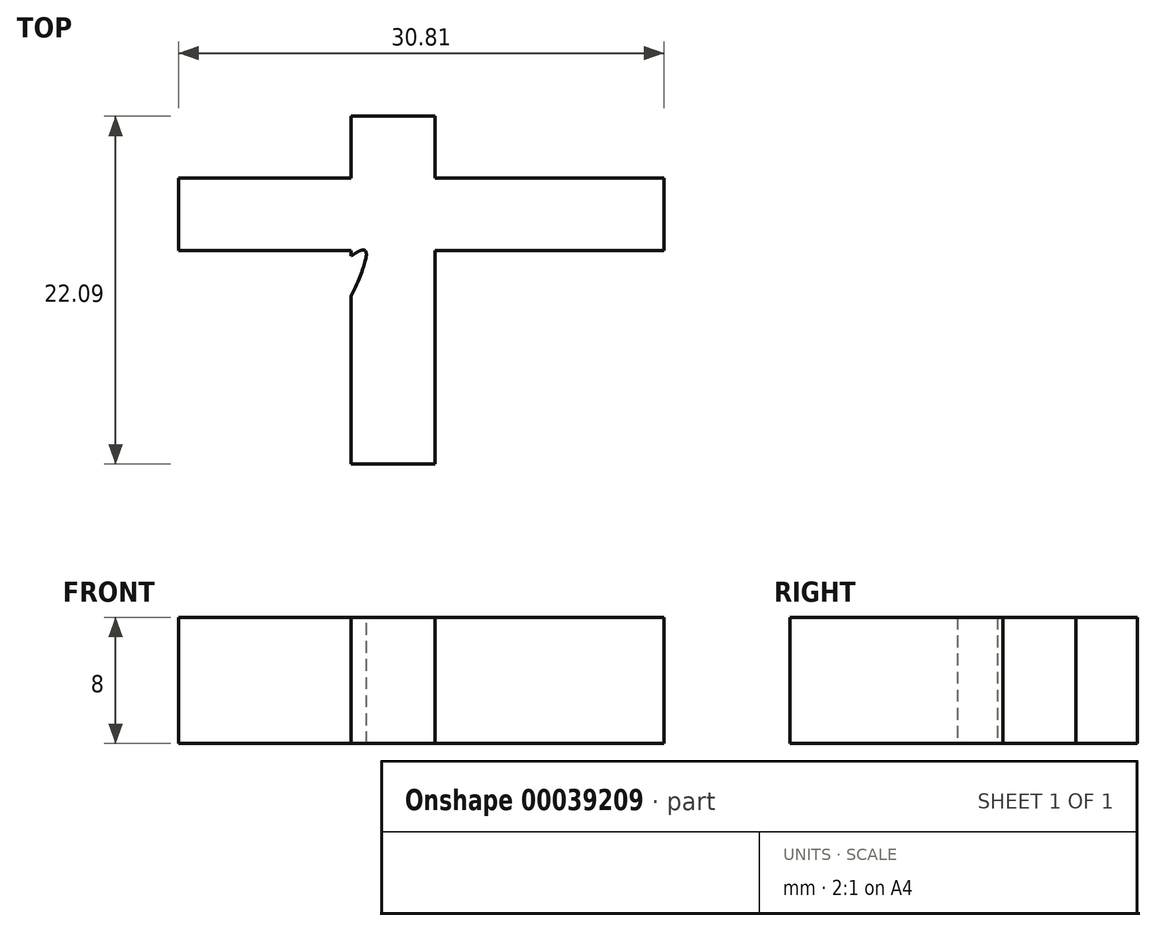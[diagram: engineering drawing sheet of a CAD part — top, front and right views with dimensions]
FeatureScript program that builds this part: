
annotation { "Feature Type Name" : "Feature", "Feature Type Description" : "" }
export const myFeature = defineFeature(function(context is Context, id is Id, definition is map)
    precondition{}
    {
        {
            var Q0;
            Q0=qCreatedBy(makeId("Top.planeOp"),FACE);
            var sketch = newSketch(context, id + "F0", { "sketchPlane" : qUnion([Q0])});
            skLineSegment(sketch, "E0.bottom", {"start": v(-13.7, 22.5) * mm, "end": v(17.11, 22.5) * mm});
            skLineSegment(sketch, "E0.top", {"start": v(-13.7, 17.89) * mm, "end": v(17.11, 17.89) * mm});
            skLineSegment(sketch, "E0.left", {"start": v(-13.7, 22.5) * mm, "end": v(-13.7, 17.89) * mm});
            skLineSegment(sketch, "E0.right", {"start": v(17.11, 22.5) * mm, "end": v(17.11, 17.89) * mm});
            skLineSegment(sketch, "E1.bottom", {"start": v(-2.74, 26.43) * mm, "end": v(2.59, 26.43) * mm});
            skLineSegment(sketch, "E1.top", {"start": v(-2.74, 4.34) * mm, "end": v(2.59, 4.34) * mm});
            skLineSegment(sketch, "E1.left", {"start": v(-2.74, 26.43) * mm, "end": v(-2.74, 4.34) * mm});
            skLineSegment(sketch, "E1.right", {"start": v(2.59, 26.43) * mm, "end": v(2.59, 4.34) * mm});
            skPoint(sketch, "E2.0.internal.snap0", {"position": v(-2.74, 15.39) * mm});
            skFitSpline(sketch, "E3.MirrorC", {"points": [v(1.84, 17.89) * mm, v(8.57, 12.75) * mm, v(13.7, 8.64) * mm, v(11.13, 5.56) * mm, v(6.51, 8.64) * mm, v(1.84, 17.89) * mm]});
            skPoint(sketch, "E4.MirrorP", {"position": v(2.74, 15.39) * mm});
            skFitSpline(sketch, "E5.MirrorC", {"points": [v(-1.84, 17.89) * mm, v(-8.57, 12.75) * mm, v(-13.7, 8.64) * mm, v(-11.13, 5.56) * mm, v(-6.51, 8.64) * mm, v(-1.84, 17.89) * mm]});
            skSolve(sketch);
        }
        {
            var Q0;
            {var subQ0=sQuery(id+"F0.wireOp",EDGE,"E1.left");var subQ3=sQuery(id+"F0.wireOp",EDGE,"E0.bottom");var subQ4=makeQuery(id+"F0.imprint","INTERSECT",VERTEX,{"derivedFrom":[subQ3,subQ0]});Q0=makeQuery(id+"F0.imprint","IMPRINT",FACE,{"disambiguationData":[TD([[makeQuery(id+"F0.imprint","IMPRINT",EDGE,{"disambiguationData":[TD([[subQ4,-1.0]])],"derivedFrom":subQ3}),-1.0]])]});}
            var Q1;
            {var subQ3=sQuery(id+"F0.wireOp",EDGE,"E1.bottom");Q1=makeQuery(id+"F0.imprint","IMPRINT",FACE,{"disambiguationData":[TD([[makeQuery(id+"F0.imprint","IMPRINT",EDGE,{"derivedFrom":subQ3}),-1.0]])]});}
            var Q2;
            {var subQ7=sQuery(id+"F0.wireOp",EDGE,"E0.left");Q2=makeQuery(id+"F0.imprint","IMPRINT",FACE,{"disambiguationData":[TD([[makeQuery(id+"F0.imprint","IMPRINT",EDGE,{"derivedFrom":subQ7}),1.0]])]});}
            var Q3;
            {var subQ1=sQuery(id+"F0.wireOp",EDGE,"E0.top");var subQ2=sQuery(id+"F0.wireOp",EDGE,"E2");var subQ5=makeQuery(id+"F0.imprint","INTERSECT",VERTEX,{"derivedFrom":[subQ1,subQ2]});Q3=makeQuery(id+"F0.imprint","IMPRINT",FACE,{"disambiguationData":[TD([[makeQuery(id+"F0.imprint","IMPRINT",EDGE,{"disambiguationData":[TD([[subQ5,-1.0]])],"derivedFrom":subQ2}),1.0]])]});}
            var Q4;
            {var subQ0=sQuery(id+"F0.wireOp",EDGE,"E3.MirrorC");var subQ1=sQuery(id+"F0.wireOp",EDGE,"E0.top");var subQ3=makeQuery(id+"F0.imprint","INTERSECT",VERTEX,{"disambiguationData":[OD(0.0)],"derivedFrom":[subQ1,subQ0]});Q4=makeQuery(id+"F0.imprint","IMPRINT",FACE,{"disambiguationData":[TD([[makeQuery(id+"F0.imprint","IMPRINT",EDGE,{"disambiguationData":[TD([[subQ3,-1.0]])],"derivedFrom":subQ1}),-1.0]])]});}
            var Q5;
            {var subQ8=sQuery(id+"F0.wireOp",EDGE,"E0.right");Q5=makeQuery(id+"F0.imprint","IMPRINT",FACE,{"disambiguationData":[TD([[makeQuery(id+"F0.imprint","IMPRINT",EDGE,{"derivedFrom":subQ8}),-1.0]])]});}
            var Q6;
            {var subQ0=sQuery(id+"F0.wireOp",EDGE,"E5.MirrorC");var subQ1=sQuery(id+"F0.wireOp",EDGE,"E1.left");var subQ3=makeQuery(id+"F0.imprint","INTERSECT",VERTEX,{"disambiguationData":[OD(0.0)],"derivedFrom":[subQ1,subQ0]});Q6=makeQuery(id+"F0.imprint","IMPRINT",FACE,{"disambiguationData":[TD([[makeQuery(id+"F0.imprint","IMPRINT",EDGE,{"disambiguationData":[TD([[subQ3,-1.0]])],"derivedFrom":subQ1}),-1.0]])]});}
            var Q7;
            {var subQ0=sQuery(id+"F0.wireOp",EDGE,"E3.MirrorC");var subQ1=sQuery(id+"F0.wireOp",EDGE,"E1.right");var subQ3=makeQuery(id+"F0.imprint","INTERSECT",VERTEX,{"disambiguationData":[OD(0.0)],"derivedFrom":[subQ1,subQ0]});Q7=makeQuery(id+"F0.imprint","IMPRINT",FACE,{"disambiguationData":[TD([[makeQuery(id+"F0.imprint","IMPRINT",EDGE,{"disambiguationData":[TD([[subQ3,-1.0]])],"derivedFrom":subQ1}),1.0]])]});}
            var Q8;
            {var subQ0=sQuery(id+"F0.wireOp",EDGE,"E5.MirrorC");var subQ1=sQuery(id+"F0.wireOp",EDGE,"E0.top");var subQ5=makeQuery(id+"F0.imprint","INTERSECT",VERTEX,{"disambiguationData":[OD(0.0)],"derivedFrom":[subQ1,subQ0]});Q8=makeQuery(id+"F0.imprint","IMPRINT",FACE,{"disambiguationData":[TD([[makeQuery(id+"F0.imprint","IMPRINT",EDGE,{"disambiguationData":[TD([[subQ5,-1.0]])],"derivedFrom":subQ1}),-1.0]])]});}
            var Q9;
            {var subQ9=sQuery(id+"F0.wireOp",EDGE,"E1.top");Q9=makeQuery(id+"F0.imprint","IMPRINT",FACE,{"disambiguationData":[TD([[makeQuery(id+"F0.imprint","IMPRINT",EDGE,{"derivedFrom":subQ9}),1.0]])]});}
            var Q10;
            {var subQ0=sQuery(id+"F0.wireOp",EDGE,"E1.right");var subQ3=sQuery(id+"F0.wireOp",EDGE,"E0.top");var subQ4=makeQuery(id+"F0.imprint","INTERSECT",VERTEX,{"derivedFrom":[subQ3,subQ0]});Q10=makeQuery(id+"F0.imprint","IMPRINT",FACE,{"disambiguationData":[TD([[makeQuery(id+"F0.imprint","IMPRINT",EDGE,{"disambiguationData":[TD([[subQ4,1.0]])],"derivedFrom":subQ3}),-1.0]])]});}
            var Q11;
            {var subQ1=sQuery(id+"F0.wireOp",EDGE,"E0.top");var subQ3=sQuery(id+"F0.wireOp",EDGE,"E1.left");var subQ5=makeQuery(id+"F0.imprint","INTERSECT",VERTEX,{"derivedFrom":[subQ1,subQ3]});Q11=makeQuery(id+"F0.imprint","IMPRINT",FACE,{"disambiguationData":[TD([[makeQuery(id+"F0.imprint","IMPRINT",EDGE,{"disambiguationData":[TD([[subQ5,-1.0]])],"derivedFrom":subQ1}),-1.0]])]});}
            var Q12;
            {var subQ0=sQuery(id+"F0.wireOp",EDGE,"E5.MirrorC");var subQ1=sQuery(id+"F0.wireOp",EDGE,"E0.top");var subQ3=makeQuery(id+"F0.imprint","INTERSECT",VERTEX,{"disambiguationData":[OD(0.0)],"derivedFrom":[subQ1,subQ0]});Q12=makeQuery(id+"F0.imprint","IMPRINT",FACE,{"disambiguationData":[TD([[makeQuery(id+"F0.imprint","IMPRINT",EDGE,{"disambiguationData":[TD([[subQ3,-1.0]])],"derivedFrom":subQ1}),1.0]])]});}
            var Q13;
            {var subQ0=sQuery(id+"F0.wireOp",EDGE,"E3.MirrorC");var subQ1=sQuery(id+"F0.wireOp",EDGE,"E0.top");var subQ3=makeQuery(id+"F0.imprint","INTERSECT",VERTEX,{"disambiguationData":[OD(0.0)],"derivedFrom":[subQ1,subQ0]});Q13=makeQuery(id+"F0.imprint","IMPRINT",FACE,{"disambiguationData":[TD([[makeQuery(id+"F0.imprint","IMPRINT",EDGE,{"disambiguationData":[TD([[subQ3,-1.0]])],"derivedFrom":subQ1}),1.0]])]});}
            extrude(context, id + "F1", {"entities" : qUnion([Q0, Q1, Q2, Q3, Q4, Q5, Q6, Q7, Q8, Q9, Q10, Q11, Q12, Q13]), "depth" : 8 * mm});
        }
    });
